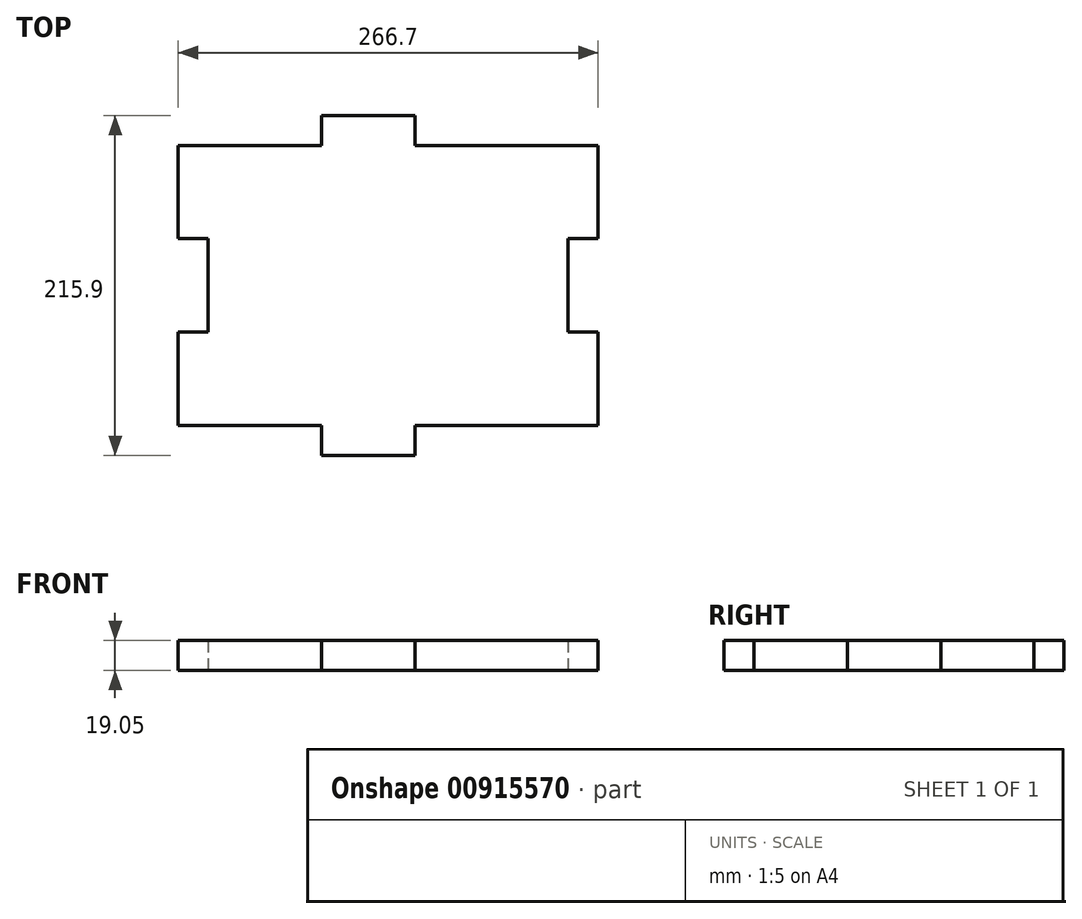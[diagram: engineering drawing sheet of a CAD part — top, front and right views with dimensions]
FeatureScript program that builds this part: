
annotation { "Feature Type Name" : "Feature", "Feature Type Description" : "" }
export const myFeature = defineFeature(function(context is Context, id is Id, definition is map)
    precondition{}
    {
        {
            var Q0;
            Q0=qCreatedBy(makeId("Top.planeOp"),FACE);
            var sketch = newSketch(context, id + "F0", { "sketchPlane" : qUnion([Q0])});
            skPoint(sketch, "E0.middle", {"position": v(0, 0) * mm});
            skLineSegment(sketch, "E1", {"start": v(-101.6, 29.72) * mm, "end": v(-120.65, 29.72) * mm});
            skLineSegment(sketch, "E2.bottom", {"start": v(-120.65, 29.72) * mm, "end": v(-101.6, 29.72) * mm});
            skLineSegment(sketch, "E2.top", {"start": v(-120.65, 88.9) * mm, "end": v(-101.6, 88.9) * mm});
            skLineSegment(sketch, "E2.left", {"start": v(-120.65, 29.72) * mm, "end": v(-120.65, 88.9) * mm});
            skLineSegment(sketch, "E3", {"start": v(-101.6, -29.6) * mm, "end": v(-120.65, -29.6) * mm});
            skLineSegment(sketch, "E4.bottom", {"start": v(-101.6, -88.9) * mm, "end": v(-120.65, -88.9) * mm});
            skLineSegment(sketch, "E4.right", {"start": v(-120.65, -88.9) * mm, "end": v(-120.65, -29.6) * mm});
            skLineSegment(sketch, "E5.bottom", {"start": v(101.6, -88.9) * mm, "end": v(120.65, -88.9) * mm});
            skLineSegment(sketch, "E6", {"start": v(-101.6, 29.72) * mm, "end": v(-101.6, -29.6) * mm});
            skLineSegment(sketch, "E7.top", {"start": v(120.65, 88.9) * mm, "end": v(101.6, 88.9) * mm});
            skLineSegment(sketch, "E8", {"start": v(0, 107.95) * mm, "end": v(29.63, 107.95) * mm});
            skLineSegment(sketch, "E9", {"start": v(0, 107.95) * mm, "end": v(-29.63, 107.95) * mm});
            skLineSegment(sketch, "E10", {"start": v(-29.63, 107.95) * mm, "end": v(-29.63, 88.9) * mm});
            skLineSegment(sketch, "E11.bottom", {"start": v(29.63, 107.95) * mm, "end": v(-29.63, 107.95) * mm});
            skLineSegment(sketch, "E11.left", {"start": v(29.63, 107.95) * mm, "end": v(29.63, 88.9) * mm});
            skLineSegment(sketch, "E12", {"start": v(-101.6, 88.9) * mm, "end": v(-29.63, 88.9) * mm});
            skLineSegment(sketch, "E13", {"start": v(29.63, 88.9) * mm, "end": v(101.6, 88.9) * mm});
            skLineSegment(sketch, "E14", {"start": v(-29.63, -88.9) * mm, "end": v(-29.63, -107.95) * mm});
            skLineSegment(sketch, "E15.bottom", {"start": v(-29.63, -107.95) * mm, "end": v(29.63, -107.95) * mm});
            skLineSegment(sketch, "E15.left", {"start": v(-29.63, -107.95) * mm, "end": v(-29.63, -88.9) * mm});
            skLineSegment(sketch, "E15.right", {"start": v(29.63, -107.95) * mm, "end": v(29.63, -88.9) * mm});
            skLineSegment(sketch, "E16", {"start": v(-101.6, -88.9) * mm, "end": v(-29.63, -88.9) * mm});
            skLineSegment(sketch, "E17", {"start": v(29.63, -88.9) * mm, "end": v(101.6, -88.9) * mm});
            skLineSegment(sketch, "E18", {"start": v(120.65, 88.9) * mm, "end": v(146.05, 88.9) * mm});
            skLineSegment(sketch, "E19", {"start": v(146.05, 29.72) * mm, "end": v(146.05, 88.9) * mm});
            skLineSegment(sketch, "E20", {"start": v(146.05, -29.6) * mm, "end": v(146.05, -88.9) * mm});
            skLineSegment(sketch, "E21", {"start": v(146.05, -88.9) * mm, "end": v(120.65, -88.9) * mm});
            skLineSegment(sketch, "E22", {"start": v(127, 29.72) * mm, "end": v(127, -29.6) * mm});
            skLineSegment(sketch, "E23", {"start": v(127, -29.6) * mm, "end": v(146.05, -29.6) * mm});
            skLineSegment(sketch, "E24", {"start": v(127, 29.72) * mm, "end": v(146.05, 29.72) * mm});
            skSolve(sketch);
        }
        {
            var Q0;
            Q0 = qSketchRegion(id + "F0", true);
            extrude(context, id + "F1", {"entities" : qUnion([Q0]), "depth" : 19.05 * mm, "offsetDistance" : 25.4 * mm});
        }
    });
